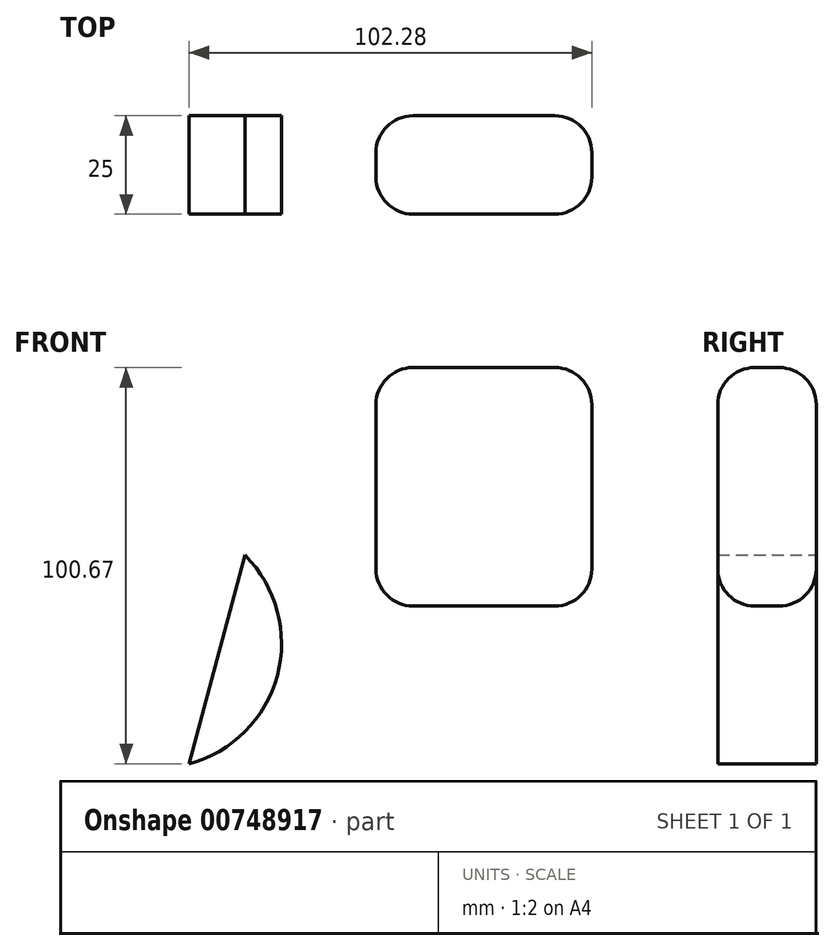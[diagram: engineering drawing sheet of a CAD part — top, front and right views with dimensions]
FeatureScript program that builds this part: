
annotation { "Feature Type Name" : "Feature", "Feature Type Description" : "" }
export const myFeature = defineFeature(function(context is Context, id is Id, definition is map)
    precondition{}
    {
        {
            var Q0;
            Q0=qCreatedBy(makeId("Front.planeOp"),FACE);
            var sketch = newSketch(context, id + "F0", { "sketchPlane" : qUnion([Q0])});
            skCircle(sketch, "E0.cCircle", {"center": v(-107.3, 6.05) * mm, "radius": 31.68 * mm});
            skLineSegment(sketch, "E0.0", {"start": v(-84.91, 28.47) * mm, "end": v(-99.07, -24.54) * mm});
            skLineSegment(sketch, "E0.1", {"start": v(-99.07, -24.54) * mm, "end": v(-137.9, 14.22) * mm});
            skLineSegment(sketch, "E0.2", {"start": v(-137.9, 14.22) * mm, "end": v(-84.91, 28.47) * mm});
            skSolve(sketch);
        }
        {
            var Q0;
            Q0=sQuery(id+"F0.wireOp",EDGE,"E0.cCircle");
            extrude(context, id + "F1", {"bodyType" : ToolBodyType.SURFACE, "surfaceEntities" : qUnion([Q0]), "depth" : 25 * mm, "offsetDistance" : 25 * mm});
        }
        {
            var Q0;
            {var subQ0=sQuery(id+"F0.wireOp",EDGE,"E0.0");Q0=makeQuery(id+"F0.imprint","IMPRINT",FACE,{"disambiguationData":[TD([[makeQuery(id+"F0.imprint","IMPRINT",EDGE,{"derivedFrom":subQ0}),1.0]])]});}
            extrude(context, id + "F2", {"entities" : qUnion([Q0]), "depth" : 25 * mm, "offsetDistance" : 25 * mm});
        }
        {
            var Q0;
            Q0=qCreatedBy(makeId("Front.planeOp"),FACE);
            var sketch = newSketch(context, id + "F3", { "sketchPlane" : qUnion([Q0])});
            skLineSegment(sketch, "E1.bottom", {"start": v(-51.64, 76.13) * mm, "end": v(3.21, 76.13) * mm});
            skLineSegment(sketch, "E1.top", {"start": v(-51.64, 15.54) * mm, "end": v(3.21, 15.54) * mm});
            skLineSegment(sketch, "E1.left", {"start": v(-51.64, 76.13) * mm, "end": v(-51.64, 15.54) * mm});
            skLineSegment(sketch, "E1.right", {"start": v(3.21, 76.13) * mm, "end": v(3.21, 15.54) * mm});
            skSolve(sketch);
        }
        {
            var Q0;
            Q0 = qSketchRegion(id + "F3", true);
            extrude(context, id + "F4", {"entities" : qUnion([Q0]), "depth" : 25 * mm, "offsetDistance" : 25 * mm});
        }
        {
            var Q0;
            Q0=makeQuery(id+"F4.opExtrude","CAP_EDGE",EDGE,{"disambiguationData":[OSD([sQuery(id+"F3.wireOp",EDGE,"E1.left")])],"isStart":false});
            var Q1;
            Q1=makeQuery(id+"F4.opExtrude","CAP_EDGE",EDGE,{"disambiguationData":[OSD([sQuery(id+"F3.wireOp",EDGE,"E1.top")])],"isStart":false});
            var Q2;
            Q2=makeQuery(id+"F4.opExtrude","CAP_EDGE",EDGE,{"disambiguationData":[OSD([sQuery(id+"F3.wireOp",EDGE,"E1.top")])],"isStart":true});
            var Q3;
            Q3=makeQuery(id+"F4.opExtrude","SWEPT_EDGE",EDGE,{"disambiguationData":[OSD([sQuery(id+"F3.wireOp",EDGE,"E1.top"),sQuery(id+"F3.wireOp",EDGE,"E1.right")])]});
            var Q4;
            Q4=makeQuery(id+"F4.opExtrude","SWEPT_EDGE",EDGE,{"disambiguationData":[OSD([sQuery(id+"F3.wireOp",EDGE,"E1.top"),sQuery(id+"F3.wireOp",EDGE,"E1.left")])]});
            var Q5;
            Q5=makeQuery(id+"F4.opExtrude","SWEPT_EDGE",EDGE,{"disambiguationData":[OSD([sQuery(id+"F3.wireOp",EDGE,"E1.bottom"),sQuery(id+"F3.wireOp",EDGE,"E1.left")])]});
            var Q6;
            Q6=makeQuery(id+"F4.opExtrude","CAP_EDGE",EDGE,{"disambiguationData":[OSD([sQuery(id+"F3.wireOp",EDGE,"E1.right")])],"isStart":false});
            var Q7;
            Q7=makeQuery(id+"F4.opExtrude","CAP_EDGE",EDGE,{"disambiguationData":[OSD([sQuery(id+"F3.wireOp",EDGE,"E1.left")])],"isStart":true});
            var Q8;
            Q8=makeQuery(id+"F4.opExtrude","CAP_EDGE",EDGE,{"disambiguationData":[OSD([sQuery(id+"F3.wireOp",EDGE,"E1.bottom")])],"isStart":false});
            var Q9;
            Q9=makeQuery(id+"F4.opExtrude","CAP_EDGE",EDGE,{"disambiguationData":[OSD([sQuery(id+"F3.wireOp",EDGE,"E1.bottom")])],"isStart":true});
            var Q10;
            Q10=makeQuery(id+"F4.opExtrude","CAP_EDGE",EDGE,{"disambiguationData":[OSD([sQuery(id+"F3.wireOp",EDGE,"E1.right")])],"isStart":true});
            var Q11;
            Q11=makeQuery(id+"F4.opExtrude","SWEPT_EDGE",EDGE,{"disambiguationData":[OSD([sQuery(id+"F3.wireOp",EDGE,"E1.bottom"),sQuery(id+"F3.wireOp",EDGE,"E1.right")])]});
            fillet(context, id + "F5", {"entities" : qUnion([Q0, Q1, Q2, Q3, Q4, Q5, Q6, Q7, Q8, Q9, Q10, Q11]), "radius" : 9.42 * mm, "tangentPropagation" : true, "allowEdgeOverflow" : false});
        }
    });
